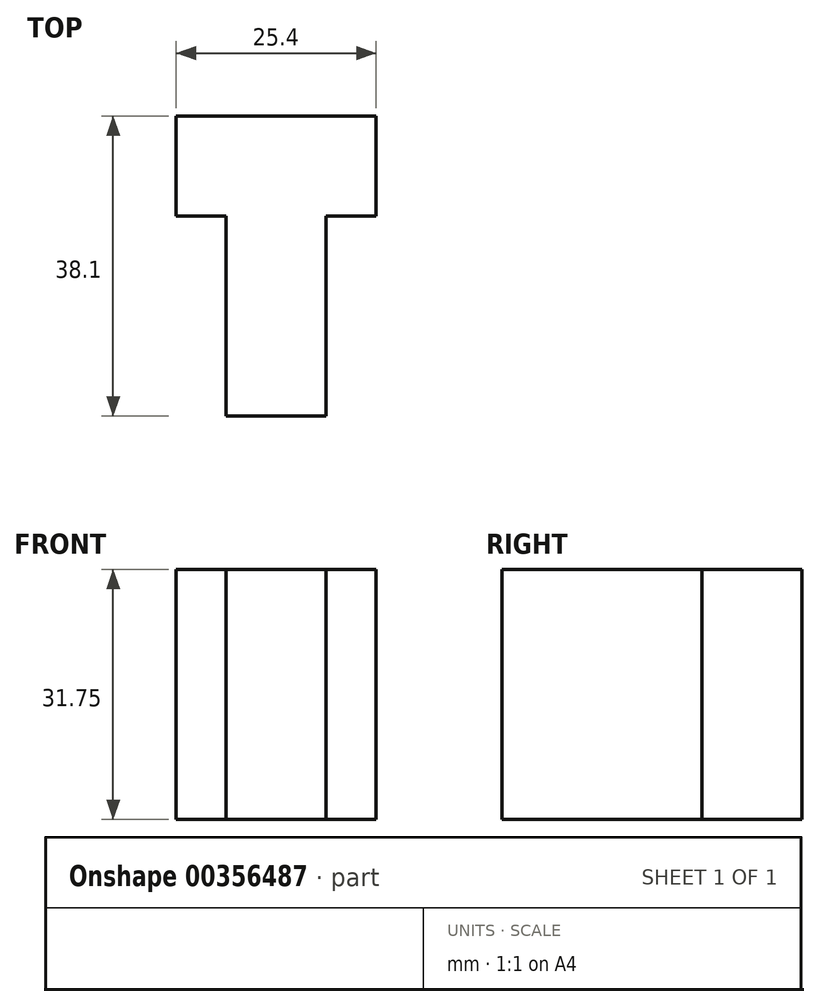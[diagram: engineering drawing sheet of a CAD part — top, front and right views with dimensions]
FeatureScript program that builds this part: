
annotation { "Feature Type Name" : "Feature", "Feature Type Description" : "" }
export const myFeature = defineFeature(function(context is Context, id is Id, definition is map)
    precondition{}
    {
        {
            var Q0;
            Q0=qCreatedBy(makeId("Top.planeOp"),FACE);
            var sketch = newSketch(context, id + "F0", { "sketchPlane" : qUnion([Q0])});
            skLineSegment(sketch, "E0", {"start": v(0, 0) * mm, "end": v(0, 25.4) * mm});
            skLineSegment(sketch, "E1", {"start": v(-6.35, 25.4) * mm, "end": v(-6.35, 38.1) * mm});
            skLineSegment(sketch, "E2", {"start": v(-6.35, 38.1) * mm, "end": v(19.05, 38.1) * mm});
            skLineSegment(sketch, "E3", {"start": v(19.05, 38.1) * mm, "end": v(19.05, 25.4) * mm});
            skLineSegment(sketch, "E4", {"start": v(19.05, 25.4) * mm, "end": v(12.7, 25.4) * mm});
            skLineSegment(sketch, "E5", {"start": v(12.7, 25.4) * mm, "end": v(12.7, 0) * mm});
            skLineSegment(sketch, "E6", {"start": v(12.7, 0) * mm, "end": v(0, 0) * mm});
            skLineSegment(sketch, "E7", {"start": v(-6.35, 25.4) * mm, "end": v(0, 25.4) * mm});
            skSolve(sketch);
        }
        {
            var Q0;
            Q0 = qSketchRegion(id + "F0", true);
            extrude(context, id + "F1", {"entities" : qUnion([Q0]), "depth" : 31.75 * mm});
        }
    });
